# Revit family: Plymold-Latitude_Metal-Barstool
name_source: partatom
category: Furniture
units: mm (PartAtom-declared; Revit-internal decimal feet)

## family parameters
Always vertical = Yes
Cut with Voids When Loaded = No
OmniClass Number = 23.40.20.00
OmniClass Title = General Furniture and Specialties
Render Appearance Source = Family Geometry
Room Calculation Point = No
Shared = No
Work Plane-Based = No

## types (2) — shared parameters
Assembly Code = E2020200
Default Elevation = 0"
Depth = 21"
FRAME MATERIAL = PLY - Onyx Black Powdercoat
GLIDES MATERIAL = PLY - Plastic Black
Height = 42 1/2"
Keynote = 12500
Manufacturer = Plymold Inc.
Product Documentation Link = https://plymold.com
Revit File Built By = https://servex-us.com
Sustainability = https://plymold.com
Type Comments = Latitude
URL = https://plymold.com
Width = 17 3/4"

## per-type parameters (varying)
| type | Description | Padded Seat | SEAT MATERIAL | Wood Seat |
| B5303SS | Wood Saddle Seat - 17.5"W x 21"D x 42.5"H | No | PLY - Wood Mahogany | Yes |
| B5303PS | Vinyl Padded Seat - 17.5"W x 21"D x 42.5"H | Yes | PLY - Vinyl - Lite Gray | No |

note: column(s) folded — value = type name in every type: Model

## geometry (parser evidence)
native form markers: Sweep x4
no freeform markers — native parametric forms only
